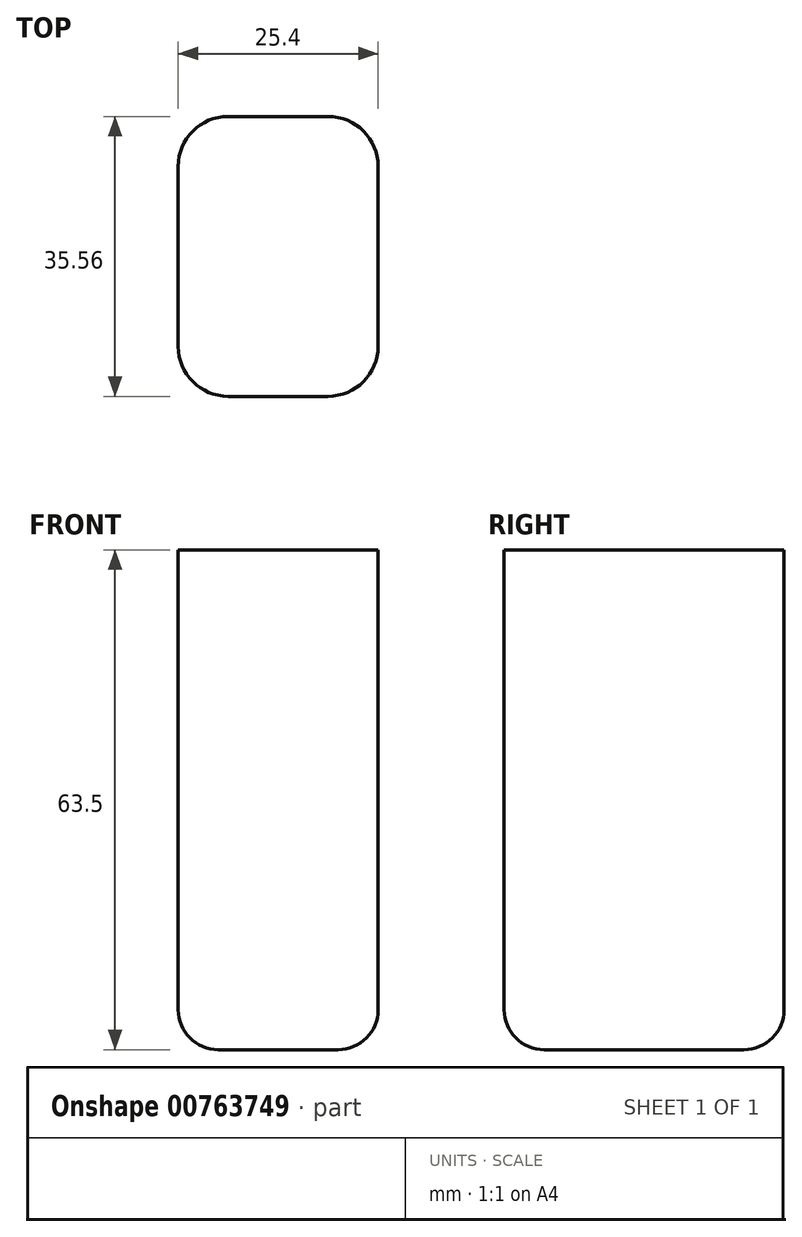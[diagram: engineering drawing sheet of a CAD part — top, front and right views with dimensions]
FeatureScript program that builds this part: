
annotation { "Feature Type Name" : "Feature", "Feature Type Description" : "" }
export const myFeature = defineFeature(function(context is Context, id is Id, definition is map)
    precondition{}
    {
        {
            var Q0;
            Q0=qCreatedBy(makeId("Front.planeOp"),FACE);
            var sketch = newSketch(context, id + "F0", { "sketchPlane" : qUnion([Q0])});
            skLineSegment(sketch, "E0.bottom", {"start": v(12.7, -31.75) * mm, "end": v(-12.7, -31.75) * mm});
            skLineSegment(sketch, "E0.top", {"start": v(12.7, 31.75) * mm, "end": v(-12.7, 31.75) * mm});
            skLineSegment(sketch, "E0.left", {"start": v(12.7, -31.75) * mm, "end": v(12.7, 31.75) * mm});
            skLineSegment(sketch, "E0.right", {"start": v(-12.7, -31.75) * mm, "end": v(-12.7, 31.75) * mm});
            skPoint(sketch, "E0.middle", {"position": v(0, 0) * mm});
            skSolve(sketch);
        }
        {
            var Q0;
            Q0=makeQuery(id+"F0.imprint","IMPRINT",FACE,{"disambiguationData":[TD([[makeQuery(id+"F0.imprint","IMPRINT",EDGE,{"derivedFrom":sQuery(id+"F0.wireOp",EDGE,"E0.bottom")}),-1.0]])]});
            extrude(context, id + "F1", {"entities" : qUnion([Q0]), "endBound" : BoundingType.SYMMETRIC, "depth" : 35.56 * mm, "offsetDistance" : 25.4 * mm});
        }
        {
            var Q0;
            Q0=makeQuery(id+"F1.opExtrude","CAP_EDGE",EDGE,{"disambiguationData":[OSD([sQuery(id+"F0.wireOp",EDGE,"E0.right")])],"isStart":false});
            var Q1;
            Q1=makeQuery(id+"F1.opExtrude","CAP_EDGE",EDGE,{"disambiguationData":[OSD([sQuery(id+"F0.wireOp",EDGE,"E0.right")])],"isStart":true});
            var Q2;
            Q2=makeQuery(id+"F1.opExtrude","CAP_EDGE",EDGE,{"disambiguationData":[OSD([sQuery(id+"F0.wireOp",EDGE,"E0.left")])],"isStart":true});
            var Q3;
            Q3=makeQuery(id+"F1.opExtrude","CAP_EDGE",EDGE,{"disambiguationData":[OSD([sQuery(id+"F0.wireOp",EDGE,"E0.left")])],"isStart":false});
            fillet(context, id + "F2", {"entities" : qUnion([Q0, Q1, Q2, Q3]), "radius" : 6.35 * mm, "tangentPropagation" : true, "allowEdgeOverflow" : false});
        }
        {
            var Q0;
            Q0=makeQuery(id+"F1.opExtrude","SWEPT_FACE",FACE,{"disambiguationData":[OSD([sQuery(id+"F0.wireOp",EDGE,"E0.bottom")])]});
            fillet(context, id + "F3", {"entities" : qUnion([Q0]), "radius" : 5.08 * mm, "tangentPropagation" : true, "allowEdgeOverflow" : false});
        }
    });
